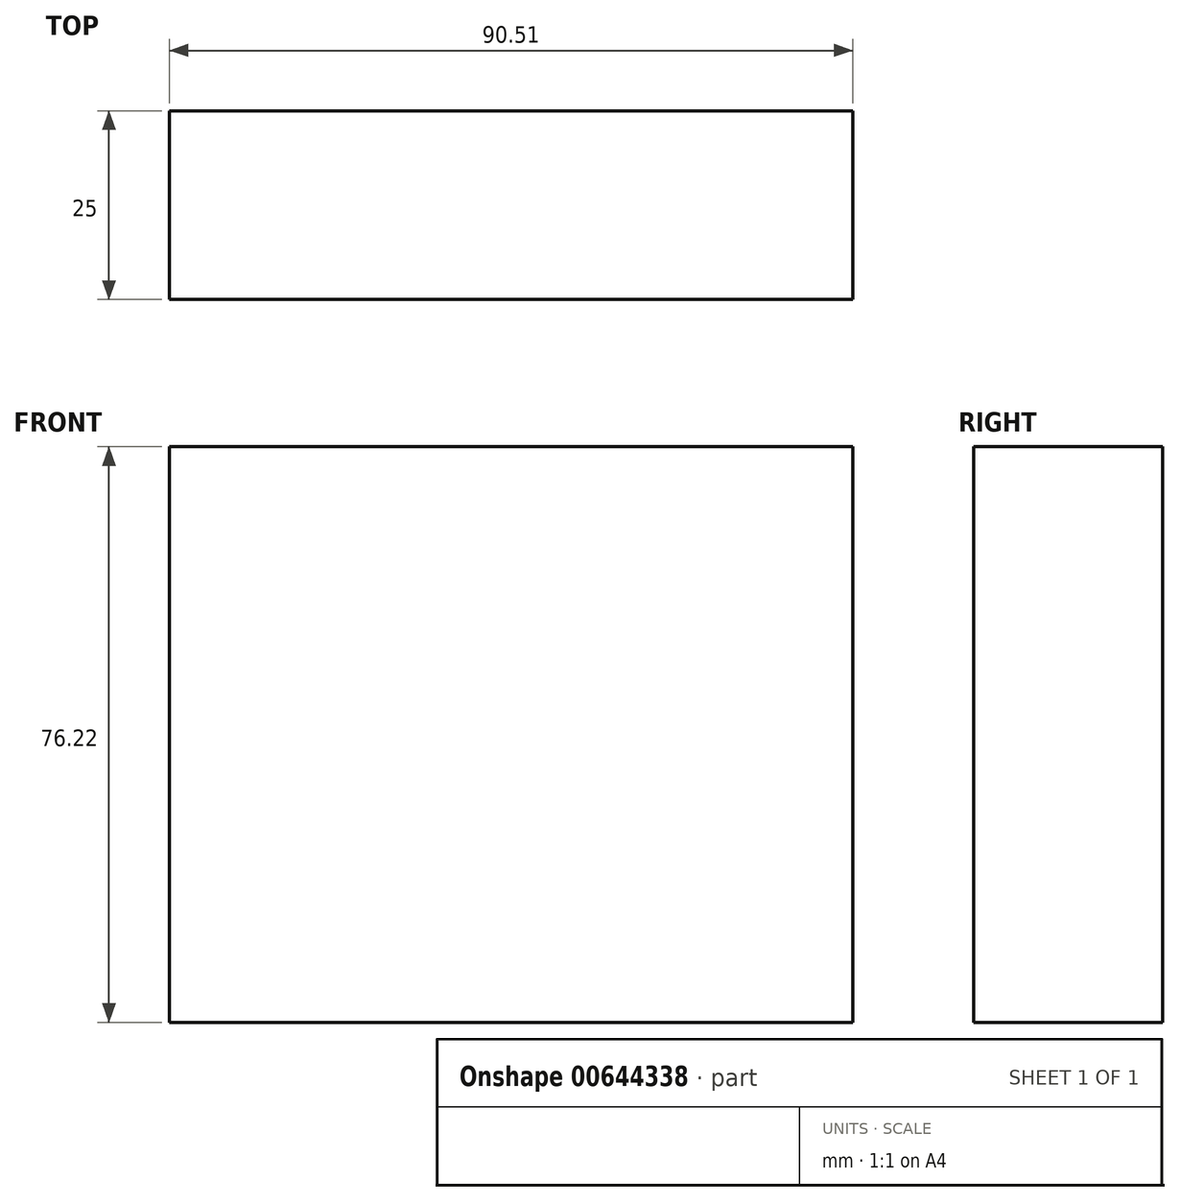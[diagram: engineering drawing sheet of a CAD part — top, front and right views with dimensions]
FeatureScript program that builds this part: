
annotation { "Feature Type Name" : "Feature", "Feature Type Description" : "" }
export const myFeature = defineFeature(function(context is Context, id is Id, definition is map)
    precondition{}
    {
        {
            var Q0;
            Q0=qCreatedBy(makeId("Front.planeOp"),FACE);
            var sketch = newSketch(context, id + "F0", { "sketchPlane" : qUnion([Q0])});
            skLineSegment(sketch, "E0.bottom", {"start": v(67.69, 47.35) * mm, "end": v(-22.82, 47.35) * mm});
            skLineSegment(sketch, "E0.top", {"start": v(67.69, -28.87) * mm, "end": v(-22.82, -28.87) * mm});
            skLineSegment(sketch, "E0.left", {"start": v(67.69, 47.35) * mm, "end": v(67.69, -28.87) * mm});
            skLineSegment(sketch, "E0.right", {"start": v(-22.82, 47.35) * mm, "end": v(-22.82, -28.87) * mm});
            skSolve(sketch);
        }
        {
            var Q0;
            Q0=makeQuery(id+"F0.imprint","IMPRINT",FACE,{"disambiguationData":[TD([[makeQuery(id+"F0.imprint","IMPRINT",EDGE,{"derivedFrom":sQuery(id+"F0.wireOp",EDGE,"E0.bottom")}),1.0]])]});
            extrude(context, id + "F1", {"entities" : qUnion([Q0]), "depth" : 25 * mm, "offsetDistance" : 25 * mm});
        }
    });
